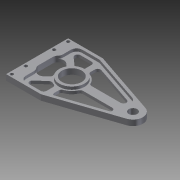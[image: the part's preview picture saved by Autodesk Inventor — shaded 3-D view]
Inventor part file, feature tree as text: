
AUTODESK INVENTOR PART (.ipt)
format: ipt  version: 2012 (Build 160160000, 160)  size: 260,608 bytes
history: native  units: in
note: dims shown in document units (in); Inventor stores cm internally (conversion verified against a paired STEP export)
features: extrude x3, fillet x3, sketch x2, hole x1
ambient origin geometry x8: Origin, YZ Plane, XZ Plane, XY Plane, X Axis, Y Axis, Z Axis, Center Point
bodies: Solid1 (feature_tree)
feature tree (9):
  sketch  "Sketch1"  dims[d0=2.75in d1=4.25in]
  extrude  "Extrusion1"  Depth=4.25in
  extrude  "Extrusion2"  Depth=0.1279in
  fillet  "Fillet1"  Radius=0.375in
  hole  "Hole1"  [1 undecoded]
  sketch  "Sketch2"  dims[d2=1.375in d6=0.1279in d7=0.375in d8=1.539in d9=0.875in d10=0.125in d11=0.0in d12=0.625in d13=0.1875in d14=0.1875in d15=0.25in d16=0.25in d17=0.125in d18=0.125in d19=0.125in d20=0.125in d21=0.125in d22=0.125in d24=0.125in d25=0.125in d26=0.25in d27=0.375in d28=0.25in d29=0.125in d30=0.0in d31=0.125in d32=0.125in d33=0.125in d35=0.125in d36=0.125in d38=0.144in d39=0.75in d40=0.25in d41=0.25in d42=0.5635in d43=1.0in d44=0.8108in d45=0.5in d46=0.125in d47=0.125in d48=0.125in d49=0.125in d51=0.125in d53=0.875in d54=0.0625in d58=0.125in d59=0.0in d62=0.75in d63=0.75in d69=0.125in d70=0.1279in d71=0.4375in d72=1.125in d73=0.25in d74=0.25in]
  extrude  "Extrusion4"  Depth=0.875in
  fillet  "Fillet6"  Radius=0.125in
  fillet  "Fillet7"  Radius=0.625in
note: 1 required parameter value undecoded (feature->parameter linkage not recoverable at this tier; creation-order binding heuristic only, values carry confidence <= 0.55)
